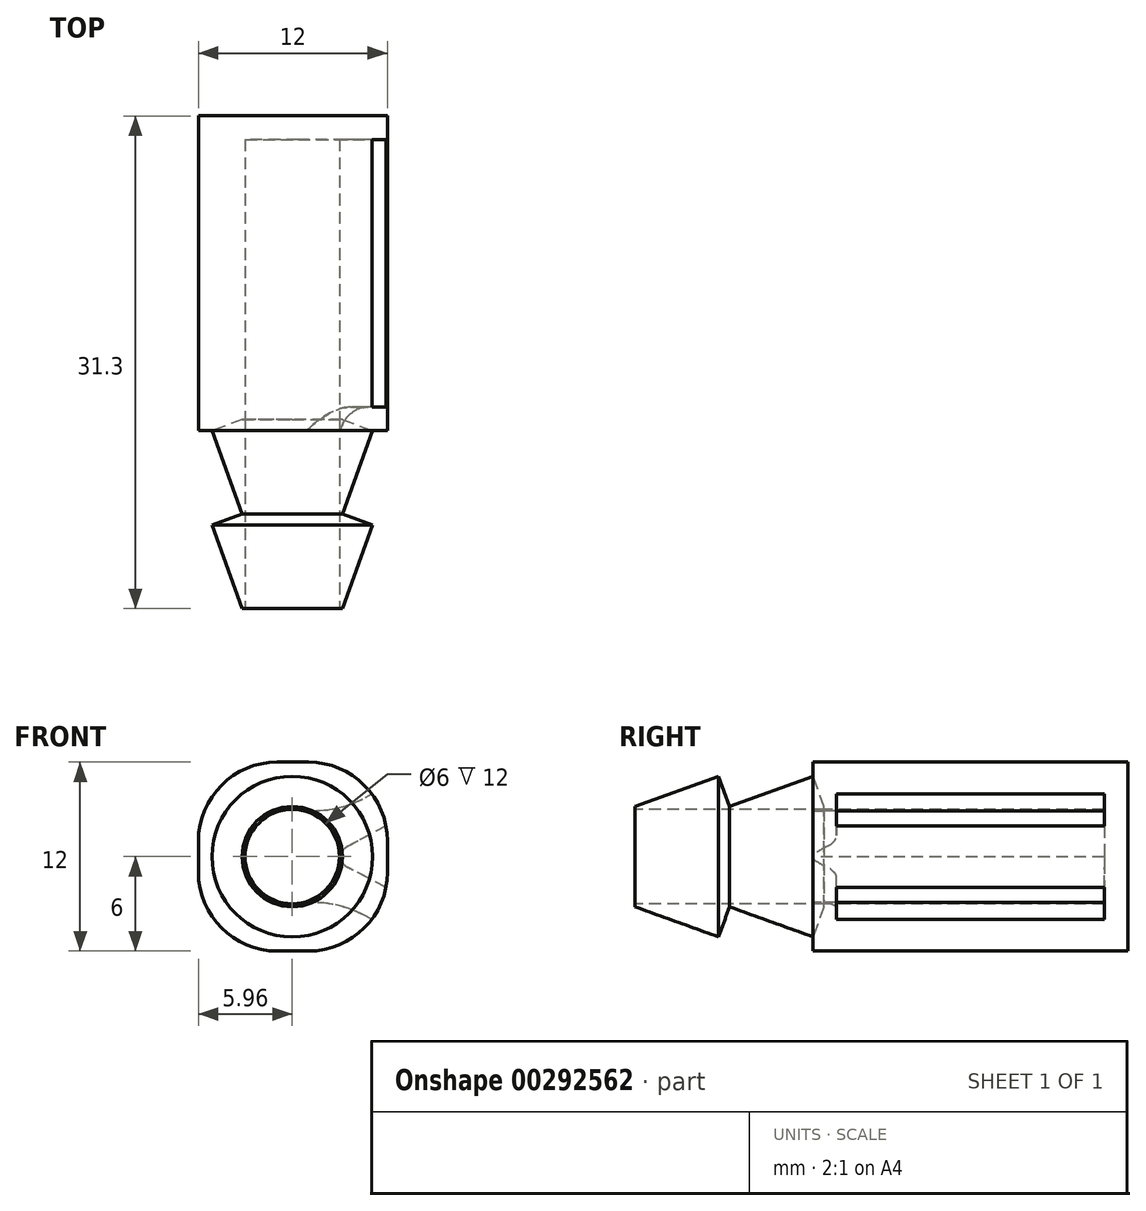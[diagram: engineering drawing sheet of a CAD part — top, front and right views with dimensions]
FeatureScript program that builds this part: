
annotation { "Feature Type Name" : "Feature", "Feature Type Description" : "" }
export const myFeature = defineFeature(function(context is Context, id is Id, definition is map)
    precondition{}
    {
        {
            var Q0;
            Q0=qCreatedBy(makeId("Right.planeOp"),FACE);
            var sketch = newSketch(context, id + "F0", { "sketchPlane" : qUnion([Q0])});
            skLineSegment(sketch, "E0", {"start": v(-22.57, 3.19) * mm, "end": v(-17.26, 5.1) * mm});
            skLineSegment(sketch, "E1", {"start": v(-17.26, 5.1) * mm, "end": v(-16.57, 3.19) * mm});
            skLineSegment(sketch, "E2", {"start": v(-16.57, 3.19) * mm, "end": v(-11.26, 5.1) * mm});
            skLineSegment(sketch, "E3", {"start": v(-11.26, 5.1) * mm, "end": v(-10.57, 3.19) * mm});
            skLineSegment(sketch, "E4", {"start": v(-10.57, 3.19) * mm, "end": v(-10.57, 0) * mm});
            skLineSegment(sketch, "E5", {"start": v(-22.57, 3.19) * mm, "end": v(-22.57, 0) * mm});
            skLineSegment(sketch, "E6", {"start": v(-22.57, 0) * mm, "end": v(-10.57, 0) * mm});
            skSolve(sketch);
        }
        {
            var Q0;
            Q0=makeQuery(id+"F0.imprint","IMPRINT",FACE,{"disambiguationData":[TD([[makeQuery(id+"F0.imprint","IMPRINT",EDGE,{"derivedFrom":sQuery(id+"F0.wireOp",EDGE,"E0")}),-1.0]])]});
            var Q1;
            Q1=sQuery(id+"F0.wireOp",EDGE,"E6");
            revolve(context, id + "F1", {"entities" : qUnion([Q0]), "axis" : qUnion([Q1]), "revolveType" : RevolveType.FULL});
        }
        {
            var Q0;
            Q0=makeQuery(id+"F1.opRevolve","SWEPT_FACE",FACE,{"disambiguationData":[OSD([sQuery(id+"F0.wireOp",EDGE,"E5")])]});
            var sketch = newSketch(context, id + "F2", { "sketchPlane" : qUnion([Q0])});
            skCircle(sketch, "E7", {"center": v(0, 0) * mm, "radius": 3 * mm});
            skSolve(sketch);
        }
        {
            var Q0;
            Q0=makeQuery(id+"F2.imprint","IMPRINT",FACE,{"disambiguationData":[TD([[makeQuery(id+"F2.imprint","IMPRINT",EDGE,{"derivedFrom":sQuery(id+"F2.wireOp",EDGE,"E7")}),1.0]])]});
            extrude(context, id + "F3", {"entities" : qUnion([Q0]), "operationType" : NewBodyOperationType.REMOVE, "oppositeDirection" : true, "depth" : 18.3 * mm});
        }
        {
            var Q0;
            Q0=qCreatedBy(makeId("Top.planeOp"),FACE);
            var sketch = newSketch(context, id + "F4", { "sketchPlane" : qUnion([Q0])});
            skLineSegment(sketch, "E8.bottom", {"start": v(-5.96, -11.27) * mm, "end": v(6.04, -11.27) * mm});
            skLineSegment(sketch, "E8.top", {"start": v(-5.96, 8.73) * mm, "end": v(6.04, 8.73) * mm});
            skLineSegment(sketch, "E8.left", {"start": v(-5.96, -11.27) * mm, "end": v(-5.96, 8.73) * mm});
            skLineSegment(sketch, "E8.right", {"start": v(6.04, -11.27) * mm, "end": v(6.04, 8.73) * mm});
            skSolve(sketch);
        }
        {
            var Q0;
            Q0=qSketchRegion(id+"F4",true);
            extrude(context, id + "F5", {"entities" : qUnion([Q0]), "depth" : 6 * mm, "hasSecondDirection" : true, "secondDirectionOppositeDirection" : true, "secondDirectionDepth" : 6 * mm});
        }
        {
            var Q0;
            Q0=makeQuery(id+"F5.opExtrude","SWEPT_FACE",FACE,{"disambiguationData":[OSD([sQuery(id+"F4.wireOp",EDGE,"E8.bottom")])]});
            var sketch = newSketch(context, id + "F6", { "sketchPlane" : qUnion([Q0])});
            skCircle(sketch, "E9", {"center": v(0, 0) * mm, "radius": 3 * mm});
            skSolve(sketch);
        }
        {
            var Q0;
            Q0=makeQuery(id+"F6.imprint","IMPRINT",FACE,{"disambiguationData":[TD([[makeQuery(id+"F6.imprint","IMPRINT",EDGE,{"derivedFrom":sQuery(id+"F6.wireOp",EDGE,"E9")}),1.0]])]});
            var Q1;
            Q1=sQuery(id+"F6.wireOp",EDGE,"E9");
            extrude(context, id + "F7", {"entities" : qUnion([Q0]), "operationType" : NewBodyOperationType.REMOVE, "surfaceEntities" : qUnion([Q1]), "oppositeDirection" : true, "depth" : 18.5 * mm});
        }
        {
            var Q0;
            Q0=makeQuery(id+"F5.opExtrude","SWEPT_FACE",FACE,{"disambiguationData":[OSD([sQuery(id+"F4.wireOp",EDGE,"E8.right")])]});
            var sketch = newSketch(context, id + "F8", { "sketchPlane" : qUnion([Q0])});
            skLineSegment(sketch, "E10.bottom", {"start": v(-9.77, 4.5) * mm, "end": v(7.23, 4.5) * mm});
            skLineSegment(sketch, "E10.top", {"start": v(-9.77, 2) * mm, "end": v(7.23, 2) * mm});
            skLineSegment(sketch, "E10.left", {"start": v(-9.77, 4.5) * mm, "end": v(-9.77, 2) * mm});
            skLineSegment(sketch, "E10.right", {"start": v(7.23, 4.5) * mm, "end": v(7.23, 2) * mm});
            skSolve(sketch);
        }
        {
            var Q0;
            Q0=makeQuery(id+"F5.opExtrude","SWEPT_FACE",FACE,{"disambiguationData":[OSD([sQuery(id+"F4.wireOp",EDGE,"E8.top")])]});
            var sketch = newSketch(context, id + "F9", { "sketchPlane" : qUnion([Q0])});
            skLineSegment(sketch, "E11", {"start": v(-0.38, 0.36) * mm, "end": v(-6.04, 3.39) * mm});
            skSolve(sketch);
        }
        {
            var Q0;
            Q0=makeQuery(id+"F8.imprint","IMPRINT",FACE,{"disambiguationData":[TD([[makeQuery(id+"F8.imprint","IMPRINT",EDGE,{"derivedFrom":sQuery(id+"F8.wireOp",EDGE,"E10.bottom")}),-1.0]])]});
            var Q1;
            Q1=sQuery(id+"F9.wireOp",EDGE,"E11");
            sweep(context, id + "F10", {"operationType" : NewBodyOperationType.REMOVE, "profiles" : qUnion([Q0]), "path" : qUnion([Q1])});
        }
        {
            var Q0;
            Q0=makeQuery(id+"F5.opExtrude","SWEPT_FACE",FACE,{"disambiguationData":[OSD([sQuery(id+"F4.wireOp",EDGE,"E8.right")])]});
            var sketch = newSketch(context, id + "F11", { "sketchPlane" : qUnion([Q0])});
            skLineSegment(sketch, "E12.bottom", {"start": v(-9.77, -2) * mm, "end": v(7.23, -2) * mm});
            skLineSegment(sketch, "E12.top", {"start": v(-9.77, -4.5) * mm, "end": v(7.23, -4.5) * mm});
            skLineSegment(sketch, "E12.left", {"start": v(-9.77, -2) * mm, "end": v(-9.77, -4.5) * mm});
            skLineSegment(sketch, "E12.right", {"start": v(7.23, -2) * mm, "end": v(7.23, -4.5) * mm});
            skSolve(sketch);
        }
        {
            var Q0;
            Q0=makeQuery(id+"F5.opExtrude","SWEPT_FACE",FACE,{"disambiguationData":[OSD([sQuery(id+"F4.wireOp",EDGE,"E8.top")])]});
            var sketch = newSketch(context, id + "F12", { "sketchPlane" : qUnion([Q0])});
            skLineSegment(sketch, "E13", {"start": v(-0.44, -0.39) * mm, "end": v(-6.04, -3.3) * mm});
            skSolve(sketch);
        }
        {
            var Q0;
            Q0=makeQuery(id+"F11.imprint","IMPRINT",FACE,{"disambiguationData":[TD([[makeQuery(id+"F11.imprint","IMPRINT",EDGE,{"derivedFrom":sQuery(id+"F11.wireOp",EDGE,"E12.bottom")}),-1.0]])]});
            var Q1;
            Q1=sQuery(id+"F12.wireOp",EDGE,"E13");
            sweep(context, id + "F13", {"operationType" : NewBodyOperationType.REMOVE, "profiles" : qUnion([Q0]), "path" : qUnion([Q1])});
        }
        {
            var Q0;
            Q0=makeQuery(id+"F5.opExtrude","CAP_EDGE",EDGE,{"disambiguationData":[OSD([sQuery(id+"F4.wireOp",EDGE,"E8.right")])],"isStart":false});
            var Q1;
            Q1=makeQuery(id+"F5.opExtrude","CAP_EDGE",EDGE,{"disambiguationData":[OSD([sQuery(id+"F4.wireOp",EDGE,"E8.left")])],"isStart":false});
            var Q2;
            Q2=makeQuery(id+"F5.opExtrude","CAP_EDGE",EDGE,{"disambiguationData":[OSD([sQuery(id+"F4.wireOp",EDGE,"E8.right")])],"isStart":true});
            var Q3;
            Q3=makeQuery(id+"F5.opExtrude","CAP_EDGE",EDGE,{"disambiguationData":[OSD([sQuery(id+"F4.wireOp",EDGE,"E8.left")])],"isStart":true});
            fillet(context, id + "F14", {"entities" : qUnion([Q0, Q1, Q2, Q3]), "radius" : 5 * mm, "tangentPropagation" : true, "allowEdgeOverflow" : false});
        }
        {
            var Q0;
            Q0=makeQuery(id+"F10.boolean.opBoolean","INTERSECT",EDGE,{"derivedFrom":[makeQuery(id+"F7.boolean.opBoolean","COPY",FACE,{"derivedFrom":makeQuery(id+"F7.opExtrude","SWEPT_FACE",FACE,{"disambiguationData":[OSD([sQuery(id+"F6.wireOp",EDGE,"E9")])]})}),makeQuery(id+"F10.opSweep","SWEPT_FACE",FACE,{"disambiguationData":[OSD([sQuery(id+"F8.wireOp",EDGE,"E10.left"),sQuery(id+"F9.wireOp",EDGE,"E11")])]})]});
            var Q1;
            Q1=makeQuery(id+"F13.boolean.opBoolean","INTERSECT",EDGE,{"derivedFrom":[makeQuery(id+"F7.boolean.opBoolean","COPY",FACE,{"derivedFrom":makeQuery(id+"F7.opExtrude","SWEPT_FACE",FACE,{"disambiguationData":[OSD([sQuery(id+"F6.wireOp",EDGE,"E9")])]})}),makeQuery(id+"F13.opSweep","SWEPT_FACE",FACE,{"disambiguationData":[OSD([sQuery(id+"F11.wireOp",EDGE,"E12.left"),sQuery(id+"F12.wireOp",EDGE,"E13")])]})]});
            fillet(context, id + "F15", {"entities" : qUnion([Q0, Q1]), "radius" : 2 * mm, "tangentPropagation" : true, "allowEdgeOverflow" : false});
        }
        {
            var Q0;
            Q0=makeQuery(id+"F13.boolean.opBoolean","INTERSECT",EDGE,{"derivedFrom":[makeQuery(id+"F7.boolean.opBoolean","COPY",FACE,{"derivedFrom":makeQuery(id+"F7.opExtrude","SWEPT_FACE",FACE,{"disambiguationData":[OSD([sQuery(id+"F6.wireOp",EDGE,"E9")])]})}),makeQuery(id+"F13.opSweep","SWEPT_FACE",FACE,{"disambiguationData":[OSD([sQuery(id+"F11.wireOp",EDGE,"E12.bottom"),sQuery(id+"F12.wireOp",EDGE,"E13")])]})]});
            var Q1;
            Q1=makeQuery(id+"F10.boolean.opBoolean","INTERSECT",EDGE,{"derivedFrom":[makeQuery(id+"F7.boolean.opBoolean","COPY",FACE,{"derivedFrom":makeQuery(id+"F7.opExtrude","SWEPT_FACE",FACE,{"disambiguationData":[OSD([sQuery(id+"F6.wireOp",EDGE,"E9")])]})}),makeQuery(id+"F10.opSweep","SWEPT_FACE",FACE,{"disambiguationData":[OSD([sQuery(id+"F8.wireOp",EDGE,"E10.top"),sQuery(id+"F9.wireOp",EDGE,"E11")])]})]});
            fillet(context, id + "F16", {"entities" : qUnion([Q0, Q1]), "radius" : 1 * mm, "tangentPropagation" : true, "allowEdgeOverflow" : false});
        }
        {
            var Q0;
            Q0=makeQuery(id+"F13.boolean.opBoolean","INTERSECT",EDGE,{"derivedFrom":[makeQuery(id+"F7.boolean.opBoolean","COPY",FACE,{"derivedFrom":makeQuery(id+"F7.opExtrude","SWEPT_FACE",FACE,{"disambiguationData":[OSD([sQuery(id+"F6.wireOp",EDGE,"E9")])]})}),makeQuery(id+"F13.opSweep","SWEPT_FACE",FACE,{"disambiguationData":[OSD([sQuery(id+"F11.wireOp",EDGE,"E12.top"),sQuery(id+"F12.wireOp",EDGE,"E13")])]})]});
            var Q1;
            Q1=makeQuery(id+"F10.boolean.opBoolean","INTERSECT",EDGE,{"derivedFrom":[makeQuery(id+"F7.boolean.opBoolean","COPY",FACE,{"derivedFrom":makeQuery(id+"F7.opExtrude","SWEPT_FACE",FACE,{"disambiguationData":[OSD([sQuery(id+"F6.wireOp",EDGE,"E9")])]})}),makeQuery(id+"F10.opSweep","SWEPT_FACE",FACE,{"disambiguationData":[OSD([sQuery(id+"F8.wireOp",EDGE,"E10.bottom"),sQuery(id+"F9.wireOp",EDGE,"E11")])]})]});
            fillet(context, id + "F17", {"entities" : qUnion([Q0, Q1]), "radius" : 7 * mm, "tangentPropagation" : true, "allowEdgeOverflow" : false});
        }
    });
